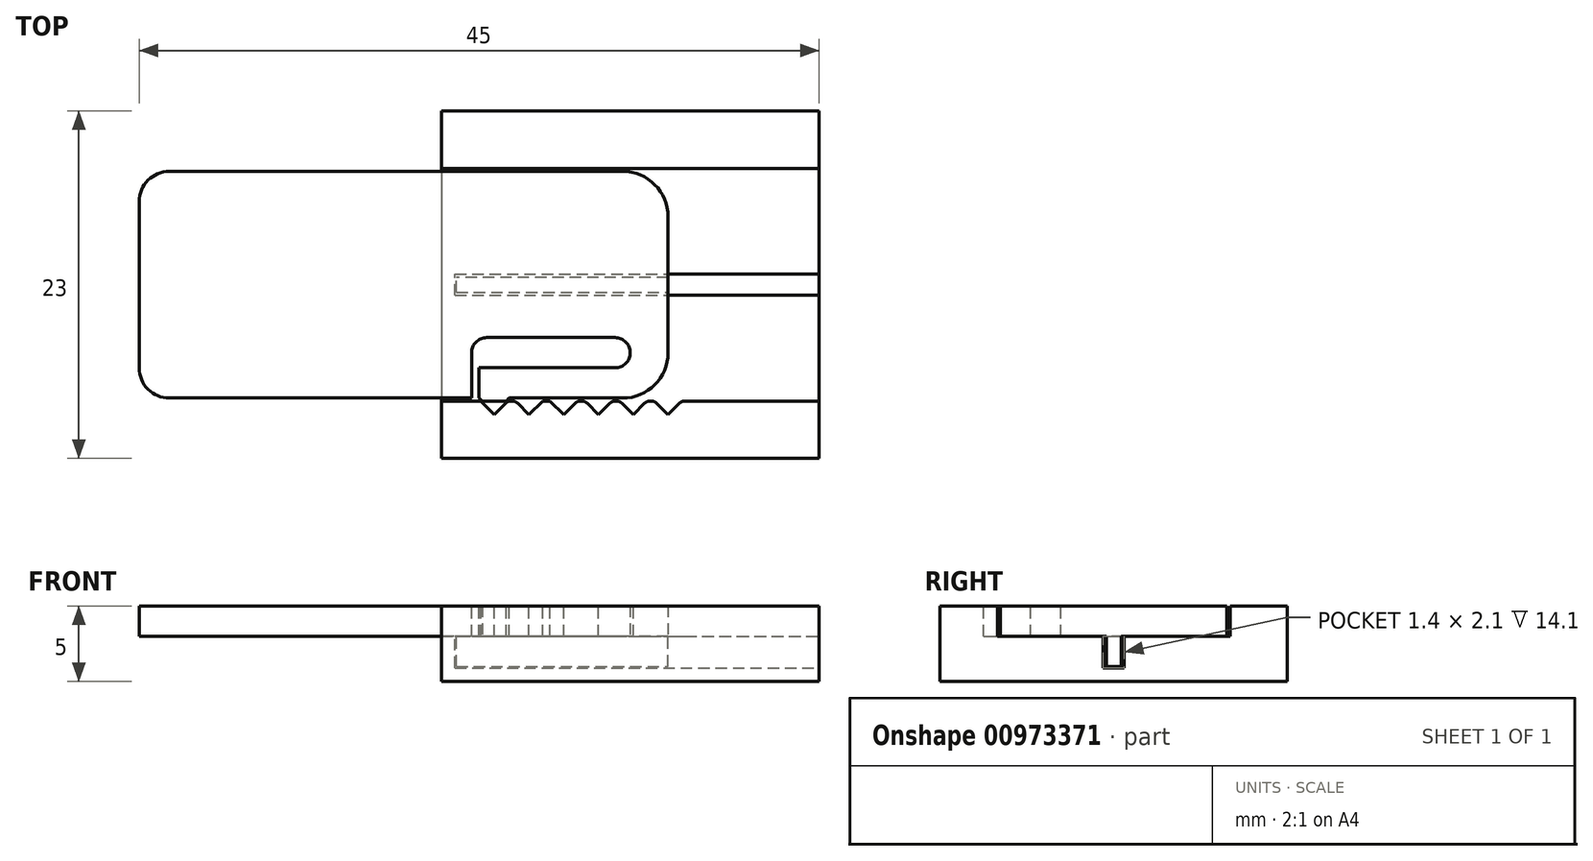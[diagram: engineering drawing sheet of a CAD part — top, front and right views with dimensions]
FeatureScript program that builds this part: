
annotation { "Feature Type Name" : "Feature", "Feature Type Description" : "" }
export const myFeature = defineFeature(function(context is Context, id is Id, definition is map)
    precondition{}
    {
        {
            var Q0;
            Q0=qCreatedBy(makeId("Top.planeOp"),FACE);
            var sketch = newSketch(context, id + "F0", { "sketchPlane" : qUnion([Q0])});
            skLineSegment(sketch, "E0.bottom", {"start": v(17.5, -7.5) * mm, "end": v(-17.5, -7.5) * mm});
            skLineSegment(sketch, "E0.top", {"start": v(17.5, 7.5) * mm, "end": v(-17.5, 7.5) * mm});
            skLineSegment(sketch, "E0.left", {"start": v(17.5, -7.5) * mm, "end": v(17.5, 7.5) * mm});
            skLineSegment(sketch, "E0.right", {"start": v(-17.5, -7.5) * mm, "end": v(-17.5, 7.5) * mm});
            skPoint(sketch, "E0.middle", {"position": v(0, 0) * mm});
            skSolve(sketch);
        }
        {
            var Q0;
            Q0 = qSketchRegion(id + "F0", true);
            extrude(context, id + "F1", {"entities" : qUnion([Q0]), "depth" : 2 * mm, "offsetDistance" : 25 * mm});
        }
        {
            var Q0;
            Q0=makeQuery(id+"F1.opExtrude","SWEPT_EDGE",EDGE,{"disambiguationData":[OSD([sQuery(id+"F0.wireOp",EDGE,"E0.bottom"),sQuery(id+"F0.wireOp",EDGE,"E0.right")])]});
            var Q1;
            Q1=makeQuery(id+"F1.opExtrude","SWEPT_EDGE",EDGE,{"disambiguationData":[OSD([sQuery(id+"F0.wireOp",EDGE,"E0.top"),sQuery(id+"F0.wireOp",EDGE,"E0.right")])]});
            fillet(context, id + "F2", {"entities" : qUnion([Q0, Q1]), "radius" : 2 * mm, "tangentPropagation" : true, "allowEdgeOverflow" : false});
        }
        {
            var Q0;
            Q0=makeQuery(id+"F1.opExtrude","CAP_FACE",FACE,{"disambiguationData":[OSD([sQuery(id+"F0.wireOp",EDGE,"E0.bottom"),sQuery(id+"F0.wireOp",EDGE,"E0.top"),sQuery(id+"F0.wireOp",EDGE,"E0.left"),sQuery(id+"F0.wireOp",EDGE,"E0.right")])],"isStart":false});
            var sketch = newSketch(context, id + "F3", { "sketchPlane" : qUnion([Q0])});
            skLineSegment(sketch, "E1", {"start": v(2.5, 7.5) * mm, "end": v(2.5, -7.5) * mm, "construction": true});
            skLineSegment(sketch, "E2", {"start": v(2.5, 0) * mm, "end": v(-17.5, 0) * mm, "construction": true});
            skLineSegment(sketch, "E3", {"start": v(2.5, -7.5) * mm, "end": v(4.5, -7.5) * mm});
            skLineSegment(sketch, "E4", {"start": v(4.5, -7.5) * mm, "end": v(4.5, -3.5) * mm});
            skLineSegment(sketch, "E5", {"start": v(4.5, -3.5) * mm, "end": v(15, -3.5) * mm});
            skLineSegment(sketch, "E6", {"start": v(15, -3.5) * mm, "end": v(15, -5.5) * mm});
            skLineSegment(sketch, "E7", {"start": v(15, -5.5) * mm, "end": v(5, -5.5) * mm});
            skLineSegment(sketch, "E8", {"start": v(5, -5.5) * mm, "end": v(5, -7.5) * mm});
            skLineSegment(sketch, "E9", {"start": v(5, -7.5) * mm, "end": v(6, -8.5) * mm});
            skLineSegment(sketch, "E10", {"start": v(6, -8.5) * mm, "end": v(7, -7.5) * mm});
            skLineSegment(sketch, "E11", {"start": v(4.5, -7.5) * mm, "end": v(5, -7.5) * mm});
            skSolve(sketch);
        }
        {
            var Q0;
            Q0 = qSketchRegion(id + "F3", true);
            extrude(context, id + "F4", {"entities" : qUnion([Q0]), "operationType" : NewBodyOperationType.REMOVE, "endBound" : BoundingType.UP_TO_NEXT, "oppositeDirection" : true, "depth" : 25 * mm, "offsetDistance" : 25 * mm});
        }
        {
            var Q0;
            {var subQ0=sQuery(id+"F3.wireOp",EDGE,"E9");Q0=makeQuery(id+"F3.imprint","IMPRINT",FACE,{"disambiguationData":[TD([[makeQuery(id+"F3.imprint","IMPRINT",EDGE,{"derivedFrom":subQ0}),1.0]])]});}
            extrude(context, id + "F5", {"entities" : qUnion([Q0]), "operationType" : NewBodyOperationType.ADD, "oppositeDirection" : true, "depth" : 2 * mm, "offsetDistance" : 25 * mm});
        }
        {
            var Q0;
            Q0=makeQuery(id+"F4.boolean.opBoolean","COPY",EDGE,{"derivedFrom":makeQuery(id+"F4.opExtrude","SWEPT_EDGE",EDGE,{"disambiguationData":[OSD([sQuery(id+"F3.wireOp",EDGE,"E6"),sQuery(id+"F3.wireOp",EDGE,"E7")])]})});
            var Q1;
            Q1=makeQuery(id+"F4.boolean.opBoolean","COPY",EDGE,{"derivedFrom":makeQuery(id+"F4.opExtrude","SWEPT_EDGE",EDGE,{"disambiguationData":[OSD([sQuery(id+"F3.wireOp",EDGE,"E5"),sQuery(id+"F3.wireOp",EDGE,"E6")])]})});
            fillet(context, id + "F6", {"entities" : qUnion([Q0, Q1]), "radius" : 1 * mm, "tangentPropagation" : true, "allowEdgeOverflow" : false});
        }
        {
            var Q0;
            Q0=makeQuery(id+"F1.opExtrude","SWEPT_EDGE",EDGE,{"disambiguationData":[OSD([sQuery(id+"F0.wireOp",EDGE,"E0.bottom"),sQuery(id+"F0.wireOp",EDGE,"E0.left")])]});
            var Q1;
            Q1=makeQuery(id+"F1.opExtrude","SWEPT_EDGE",EDGE,{"disambiguationData":[OSD([sQuery(id+"F0.wireOp",EDGE,"E0.top"),sQuery(id+"F0.wireOp",EDGE,"E0.left")])]});
            fillet(context, id + "F7", {"entities" : qUnion([Q0, Q1]), "radius" : 3 * mm, "tangentPropagation" : true, "allowEdgeOverflow" : false});
        }
        {
            var Q0;
            Q0=makeQuery(id+"F4.boolean.opBoolean","COPY",EDGE,{"derivedFrom":makeQuery(id+"F4.opExtrude","SWEPT_EDGE",EDGE,{"disambiguationData":[OSD([sQuery(id+"F3.wireOp",EDGE,"E4"),sQuery(id+"F3.wireOp",EDGE,"E5")])]})});
            var Q1;
            Q1=makeQuery(id+"FD6CfTirK5IxJer_1.1.F4.boolean.opBoolean","COPY",EDGE,{"derivedFrom":makeQuery(id+"FD6CfTirK5IxJer_1.1.F4.opExtrude","SWEPT_EDGE",EDGE,{"disambiguationData":[OSD([sQuery(id+"F3.wireOp",EDGE,"E4"),sQuery(id+"F3.wireOp",EDGE,"E5")])]})});
            fillet(context, id + "F8", {"entities" : qUnion([Q0, Q1]), "radius" : 1 * mm, "tangentPropagation" : true, "allowEdgeOverflow" : false});
        }
        {
            var Q0;
            {var subQ0=sQuery(id+"F3.wireOp",EDGE,"E10");var subQ1=sQuery(id+"F3.wireOp",EDGE,"E9");var subQ2=sQuery(id+"F0.wireOp",EDGE,"E0.bottom");Q0=makeQuery(id+"FD6CfTirK5IxJer_1.1.F5.boolean.opBoolean","MERGE",FACE,{"derivedFrom":[makeQuery(id+"F5.boolean.opBoolean","MERGE",FACE,{"derivedFrom":[makeQuery(id+"F1.opExtrude","CAP_FACE",FACE,{"disambiguationData":[OSD([subQ2,sQuery(id+"F0.wireOp",EDGE,"E0.top"),sQuery(id+"F0.wireOp",EDGE,"E0.left"),sQuery(id+"F0.wireOp",EDGE,"E0.right")])],"isStart":true}),makeQuery(id+"F5.opExtrude","CAP_FACE",FACE,{"disambiguationData":[OSD([subQ2,subQ1,subQ0])],"isStart":false})]}),makeQuery(id+"FD6CfTirK5IxJer_1.1.F5.opExtrude","CAP_FACE",FACE,{"disambiguationData":[OSD([subQ2,subQ1,subQ0])],"isStart":false})]});}
            var sketch = newSketch(context, id + "F9", { "sketchPlane" : qUnion([Q0])});
            skLineSegment(sketch, "E12.left", {"start": v(17.5, 0.5) * mm, "end": v(17.5, -0.5) * mm});
            skLineSegment(sketch, "E12.right", {"start": v(3.5, 0.5) * mm, "end": v(3.5, -0.5) * mm});
            skPoint(sketch, "E12.middle", {"position": v(0, 0) * mm});
            skLineSegment(sketch, "E13", {"start": v(3.5, 0.5) * mm, "end": v(17.5, 0.5) * mm});
            skLineSegment(sketch, "E14", {"start": v(17.5, -0.5) * mm, "end": v(3.5, -0.5) * mm});
            skLineSegment(sketch, "E15", {"start": v(0, 0) * mm, "end": v(17.5, 0) * mm, "construction": true});
            skSolve(sketch);
        }
        {
            var Q0;
            Q0 = qSketchRegion(id + "F9", true);
            extrude(context, id + "F10", {"entities" : qUnion([Q0]), "operationType" : NewBodyOperationType.ADD, "depth" : 2 * mm, "offsetDistance" : 25 * mm});
        }
        {
            var Q0;
            Q0=makeQuery(id+"F10.boolean.opBoolean","MERGE",FACE,{"derivedFrom":[makeQuery(id+"F1.opExtrude","SWEPT_FACE",FACE,{"disambiguationData":[OSD([sQuery(id+"F0.wireOp",EDGE,"E0.left")])]}),makeQuery(id+"F10.opExtrude","SWEPT_FACE",FACE,{"disambiguationData":[OSD([sQuery(id+"F9.wireOp",EDGE,"E12.left")])]})]});
            var sketch = newSketch(context, id + "F11", { "sketchPlane" : qUnion([Q0])});
            skLineSegment(sketch, "E16.0", {"start": v(0.5, -2) * mm, "end": v(0.5, 0) * mm});
            skLineSegment(sketch, "E16.1", {"start": v(-0.5, -2) * mm, "end": v(0.5, -2) * mm});
            skLineSegment(sketch, "E16.2", {"start": v(-0.5, -2) * mm, "end": v(-0.5, 0) * mm});
            skLineSegment(sketch, "E16.3", {"start": v(-4.5, 0) * mm, "end": v(-0.5, 0) * mm});
            skLineSegment(sketch, "E16.4", {"start": v(-4.5, 0) * mm, "end": v(-7.5, 0) * mm});
            skLineSegment(sketch, "E16.5", {"start": v(-8.5, 0) * mm, "end": v(-7.5, 0) * mm});
            skLineSegment(sketch, "E16.6", {"start": v(7.5, 0) * mm, "end": v(4.5, 0) * mm});
            skLineSegment(sketch, "E16.7", {"start": v(0.5, 0) * mm, "end": v(4.5, 0) * mm});
            skLineSegment(sketch, "E16.8", {"start": v(8.5, 0) * mm, "end": v(7.5, 0) * mm});
            skLineSegment(sketch, "E17.0", {"start": v(-0.7, -2) * mm, "end": v(-0.7, 0) * mm});
            skLineSegment(sketch, "E18.0", {"start": v(-0.5, -2.1) * mm, "end": v(0.5, -2.1) * mm});
            skLineSegment(sketch, "E19.0", {"start": v(0.7, -2) * mm, "end": v(0.7, 0) * mm});
            skLineSegment(sketch, "E20", {"start": v(-0.7, -2) * mm, "end": v(-0.7, -2.1) * mm});
            skLineSegment(sketch, "E21", {"start": v(-0.7, -2.1) * mm, "end": v(-0.5, -2.1) * mm});
            skLineSegment(sketch, "E22", {"start": v(0.5, -2.1) * mm, "end": v(0.7, -2.1) * mm});
            skLineSegment(sketch, "E23", {"start": v(0.7, -2.1) * mm, "end": v(0.7, -2) * mm});
            skLineSegment(sketch, "E24", {"start": v(-7.5, 0) * mm, "end": v(-7.5, 2) * mm, "construction": true});
            skLineSegment(sketch, "E25", {"start": v(-7.5, 2) * mm, "end": v(-11.5, 2) * mm});
            skLineSegment(sketch, "E26", {"start": v(-11.5, 2) * mm, "end": v(-11.5, -3) * mm});
            skLineSegment(sketch, "E27", {"start": v(7.5, 0) * mm, "end": v(7.5, 2) * mm, "construction": true});
            skLineSegment(sketch, "E28", {"start": v(7.5, 2) * mm, "end": v(11.5, 2) * mm});
            skLineSegment(sketch, "E29", {"start": v(11.5, 2) * mm, "end": v(11.5, -3) * mm});
            skLineSegment(sketch, "E30", {"start": v(11.5, -3) * mm, "end": v(-11.5, -3) * mm});
            skLineSegment(sketch, "E31.0", {"start": v(-7.7, 0) * mm, "end": v(-7.7, 2) * mm});
            skLineSegment(sketch, "E32.0", {"start": v(7.7, 0) * mm, "end": v(7.7, 2) * mm});
            skSolve(sketch);
        }
        {
            var Q0;
            {var subQ2=sQuery(id+"F11.wireOp",EDGE,"E16.4");Q0=makeQuery(id+"F11.imprint","IMPRINT",FACE,{"disambiguationData":[TD([[makeQuery(id+"F11.imprint","IMPRINT",EDGE,{"derivedFrom":subQ2}),1.0]])]});}
            extrude(context, id + "F12", {"entities" : qUnion([Q0]), "oppositeDirection" : true, "depth" : 15 * mm, "offsetDistance" : 25 * mm, "hasSecondDirection" : true, "secondDirectionOppositeDirection" : false, "secondDirectionDepth" : 10 * mm});
        }
        {
            var Q0;
            Q0=makeQuery(id+"F12.opExtrude","CAP_FACE",FACE,{"disambiguationData":[OSD([sQuery(id+"F11.wireOp",EDGE,"E16.3"),sQuery(id+"F11.wireOp",EDGE,"E16.4"),sQuery(id+"F11.wireOp",EDGE,"E16.5"),sQuery(id+"F11.wireOp",EDGE,"E16.6"),sQuery(id+"F11.wireOp",EDGE,"E16.7"),sQuery(id+"F11.wireOp",EDGE,"E16.8"),sQuery(id+"F11.wireOp",EDGE,"E17.0"),sQuery(id+"F11.wireOp",EDGE,"E18.0"),sQuery(id+"F11.wireOp",EDGE,"E19.0"),sQuery(id+"F11.wireOp",EDGE,"E20"),sQuery(id+"F11.wireOp",EDGE,"E21"),sQuery(id+"F11.wireOp",EDGE,"E22"),sQuery(id+"F11.wireOp",EDGE,"E23"),sQuery(id+"F11.wireOp",EDGE,"E25"),sQuery(id+"F11.wireOp",EDGE,"E26"),sQuery(id+"F11.wireOp",EDGE,"E28"),sQuery(id+"F11.wireOp",EDGE,"E29"),sQuery(id+"F11.wireOp",EDGE,"E30"),sQuery(id+"F11.wireOp",EDGE,"E31.0"),sQuery(id+"F11.wireOp",EDGE,"E32.0")])],"isStart":false});
            var sketch = newSketch(context, id + "F13", { "sketchPlane" : qUnion([Q0])});
            skLineSegment(sketch, "E33.bottom", {"start": v(0.7, -2.1) * mm, "end": v(-0.7, -2.1) * mm});
            skLineSegment(sketch, "E33.top", {"start": v(0.7, 0) * mm, "end": v(-0.7, 0) * mm});
            skLineSegment(sketch, "E33.left", {"start": v(0.7, -2.1) * mm, "end": v(0.7, 0) * mm});
            skLineSegment(sketch, "E33.right", {"start": v(-0.7, -2.1) * mm, "end": v(-0.7, 0) * mm});
            skSolve(sketch);
        }
        {
            var Q0;
            Q0=makeQuery(id+"F13.imprint","IMPRINT",FACE,{"disambiguationData":[TD([[makeQuery(id+"F13.imprint","IMPRINT",EDGE,{"derivedFrom":sQuery(id+"F13.wireOp",EDGE,"E33.bottom")}),-1.0]])]});
            extrude(context, id + "F14", {"entities" : qUnion([Q0]), "operationType" : NewBodyOperationType.ADD, "oppositeDirection" : true, "depth" : .9 * mm, "offsetDistance" : 25 * mm});
        }
        {
            var Q0;
            Q0=makeQuery(id+"F12.opExtrude","SWEPT_FACE",FACE,{"disambiguationData":[OSD([sQuery(id+"F11.wireOp",EDGE,"E25")])]});
            var sketch = newSketch(context, id + "F15", { "sketchPlane" : qUnion([Q0])});
            skLineSegment(sketch, "E34", {"start": v(6, -7.7) * mm, "end": v(6, -8.6) * mm, "construction": true});
            skLineSegment(sketch, "E35", {"start": v(6, -8.6) * mm, "end": v(5.1, -7.7) * mm});
            skLineSegment(sketch, "E36", {"start": v(6, -8.6) * mm, "end": v(6.9, -7.7) * mm});
            skLineSegment(sketch, "E37", {"start": v(6.9, -7.7) * mm, "end": v(7.4, -7.7) * mm});
            skLineSegment(sketch, "E38", {"start": v(8.3, -8.6) * mm, "end": v(7.4, -7.7) * mm});
            skLineSegment(sketch, "E39", {"start": v(8.3, -8.6) * mm, "end": v(9.2, -7.7) * mm});
            skLineSegment(sketch, "E40", {"start": v(9.2, -7.7) * mm, "end": v(9.7, -7.7) * mm});
            skLineSegment(sketch, "E41", {"start": v(10.6, -8.6) * mm, "end": v(9.7, -7.7) * mm});
            skLineSegment(sketch, "E42", {"start": v(10.6, -8.6) * mm, "end": v(11.5, -7.7) * mm});
            skLineSegment(sketch, "E43", {"start": v(11.5, -7.7) * mm, "end": v(12, -7.7) * mm});
            skLineSegment(sketch, "E44", {"start": v(12.9, -8.6) * mm, "end": v(12, -7.7) * mm});
            skLineSegment(sketch, "E45", {"start": v(12.9, -8.6) * mm, "end": v(13.8, -7.7) * mm});
            skLineSegment(sketch, "E46", {"start": v(13.8, -7.7) * mm, "end": v(14.3, -7.7) * mm});
            skLineSegment(sketch, "E47", {"start": v(15.2, -8.6) * mm, "end": v(14.3, -7.7) * mm});
            skLineSegment(sketch, "E48", {"start": v(15.2, -8.6) * mm, "end": v(16.1, -7.7) * mm});
            skLineSegment(sketch, "E49", {"start": v(16.1, -7.7) * mm, "end": v(16.6, -7.7) * mm});
            skLineSegment(sketch, "E50", {"start": v(17.5, -8.6) * mm, "end": v(16.6, -7.7) * mm});
            skLineSegment(sketch, "E51", {"start": v(17.5, -8.6) * mm, "end": v(18.4, -7.7) * mm});
            skLineSegment(sketch, "E52", {"start": v(5.1, -7.7) * mm, "end": v(18.4, -7.7) * mm});
            skSolve(sketch);
        }
        {
            var Q0;
            Q0 = qSketchRegion(id + "F15", true);
            extrude(context, id + "F16", {"entities" : qUnion([Q0]), "operationType" : NewBodyOperationType.REMOVE, "oppositeDirection" : true, "depth" : 2 * mm, "offsetDistance" : 25 * mm});
        }
        {
            var Q0;
            Q0=makeQuery(id+"F16.boolean.opBoolean","COPY",EDGE,{"derivedFrom":makeQuery(id+"F16.opExtrude","SWEPT_EDGE",EDGE,{"disambiguationData":[OSD([sQuery(id+"F15.wireOp",EDGE,"E36"),sQuery(id+"F15.wireOp",EDGE,"E52")])]})});
            var Q1;
            Q1=makeQuery(id+"F16.boolean.opBoolean","COPY",EDGE,{"derivedFrom":makeQuery(id+"F16.opExtrude","SWEPT_EDGE",EDGE,{"disambiguationData":[OSD([sQuery(id+"F15.wireOp",EDGE,"E38"),sQuery(id+"F15.wireOp",EDGE,"E52")])]})});
            var Q2;
            Q2=makeQuery(id+"F16.boolean.opBoolean","COPY",EDGE,{"derivedFrom":makeQuery(id+"F16.opExtrude","SWEPT_EDGE",EDGE,{"disambiguationData":[OSD([sQuery(id+"F15.wireOp",EDGE,"E39"),sQuery(id+"F15.wireOp",EDGE,"E52")])]})});
            var Q3;
            Q3=makeQuery(id+"F16.boolean.opBoolean","COPY",EDGE,{"derivedFrom":makeQuery(id+"F16.opExtrude","SWEPT_EDGE",EDGE,{"disambiguationData":[OSD([sQuery(id+"F15.wireOp",EDGE,"E41"),sQuery(id+"F15.wireOp",EDGE,"E52")])]})});
            var Q4;
            Q4=makeQuery(id+"F16.boolean.opBoolean","COPY",EDGE,{"derivedFrom":makeQuery(id+"F16.opExtrude","SWEPT_EDGE",EDGE,{"disambiguationData":[OSD([sQuery(id+"F15.wireOp",EDGE,"E42"),sQuery(id+"F15.wireOp",EDGE,"E52")])]})});
            var Q5;
            Q5=makeQuery(id+"F16.boolean.opBoolean","COPY",EDGE,{"derivedFrom":makeQuery(id+"F16.opExtrude","SWEPT_EDGE",EDGE,{"disambiguationData":[OSD([sQuery(id+"F15.wireOp",EDGE,"E44"),sQuery(id+"F15.wireOp",EDGE,"E52")])]})});
            var Q6;
            Q6=makeQuery(id+"F16.boolean.opBoolean","COPY",EDGE,{"derivedFrom":makeQuery(id+"F16.opExtrude","SWEPT_EDGE",EDGE,{"disambiguationData":[OSD([sQuery(id+"F15.wireOp",EDGE,"E45"),sQuery(id+"F15.wireOp",EDGE,"E52")])]})});
            var Q7;
            Q7=makeQuery(id+"F16.boolean.opBoolean","COPY",EDGE,{"derivedFrom":makeQuery(id+"F16.opExtrude","SWEPT_EDGE",EDGE,{"disambiguationData":[OSD([sQuery(id+"F15.wireOp",EDGE,"E47"),sQuery(id+"F15.wireOp",EDGE,"E52")])]})});
            var Q8;
            Q8=makeQuery(id+"F16.boolean.opBoolean","COPY",EDGE,{"derivedFrom":makeQuery(id+"F16.opExtrude","SWEPT_EDGE",EDGE,{"disambiguationData":[OSD([sQuery(id+"F15.wireOp",EDGE,"E48"),sQuery(id+"F15.wireOp",EDGE,"E52")])]})});
            var Q9;
            Q9=makeQuery(id+"F16.boolean.opBoolean","COPY",EDGE,{"derivedFrom":makeQuery(id+"F16.opExtrude","SWEPT_EDGE",EDGE,{"disambiguationData":[OSD([sQuery(id+"F15.wireOp",EDGE,"E50"),sQuery(id+"F15.wireOp",EDGE,"E52")])]})});
            var Q10;
            Q10=makeQuery(id+"F16.boolean.opBoolean","COPY",EDGE,{"derivedFrom":makeQuery(id+"F16.opExtrude","SWEPT_EDGE",EDGE,{"disambiguationData":[OSD([sQuery(id+"F11.wireOp",EDGE,"E25"),sQuery(id+"F11.wireOp",EDGE,"E31.0"),sQuery(id+"F15.wireOp",EDGE,"E51"),sQuery(id+"F15.wireOp",EDGE,"E52")])]})});
            fillet(context, id + "F17", {"entities" : qUnion([Q0, Q1, Q2, Q3, Q4, Q5, Q6, Q7, Q8, Q9, Q10]), "radius" : .5 * mm, "tangentPropagation" : true, "allowEdgeOverflow" : false});
        }
    });
